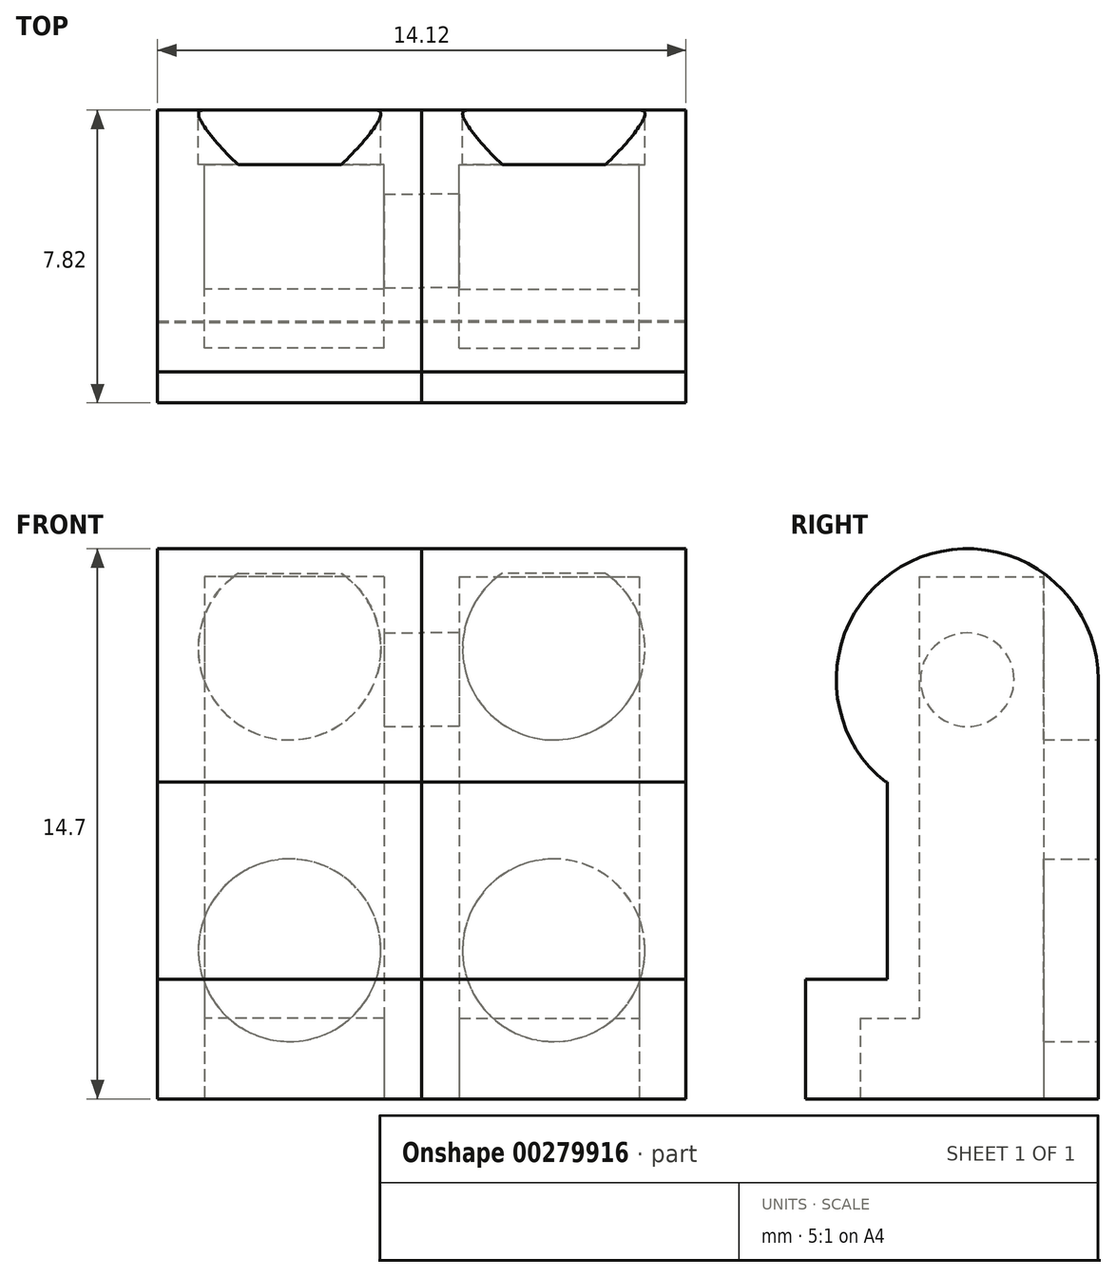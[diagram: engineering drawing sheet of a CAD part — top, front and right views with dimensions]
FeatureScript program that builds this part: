
annotation { "Feature Type Name" : "Feature", "Feature Type Description" : "" }
export const myFeature = defineFeature(function(context is Context, id is Id, definition is map)
    precondition{}
    {
        {
            var Q0;
            Q0=qCreatedBy(makeId("Right.planeOp"),FACE);
            var sketch = newSketch(context, id + "F0", { "sketchPlane" : qUnion([Q0])});
            skLineSegment(sketch, "E0.bottom", {"start": v(-3.9, 7.35) * mm, "end": v(3.91, 7.35) * mm});
            skLineSegment(sketch, "E0.top", {"start": v(-3.91, -7.35) * mm, "end": v(3.9, -7.35) * mm});
            skLineSegment(sketch, "E0.left", {"start": v(-3.9, 7.35) * mm, "end": v(-3.91, -7.35) * mm});
            skLineSegment(sketch, "E0.right", {"start": v(3.91, 7.35) * mm, "end": v(3.9, -7.35) * mm});
            skPoint(sketch, "E0.middle", {"position": v(0, 0) * mm});
            skCircle(sketch, "E1", {"center": v(0.41, 3.85) * mm, "radius": 3.5 * mm});
            skLineSegment(sketch, "E2.bottom", {"start": v(-3.91, 1.11) * mm, "end": v(-1.73, 1.11) * mm});
            skLineSegment(sketch, "E2.top", {"start": v(-3.91, -4.16) * mm, "end": v(-1.73, -4.16) * mm});
            skLineSegment(sketch, "E2.left", {"start": v(-3.9, 1.11) * mm, "end": v(-3.9, -4.16) * mm});
            skLineSegment(sketch, "E2.right", {"start": v(-1.73, 1.11) * mm, "end": v(-1.73, -4.16) * mm});
            skSolve(sketch);
        }
        {
            var Q0;
            {var subQ0=sQuery(id+"F0.wireOp",EDGE,"E1");var subQ4=makeQuery(id+"F0.imprint","INTERSECT",VERTEX,{"derivedFrom":[sQuery(id+"F0.wireOp",EDGE,"E0.bottom"),subQ0]});Q0=makeQuery(id+"F0.imprint","IMPRINT",FACE,{"disambiguationData":[TD([[makeQuery(id+"F0.imprint","IMPRINT",EDGE,{"disambiguationData":[TD([[subQ4,1.0]])],"derivedFrom":subQ0}),1.0]])]});}
            var Q1;
            {var subQ5=sQuery(id+"F0.wireOp",EDGE,"E0.top");Q1=makeQuery(id+"F0.imprint","IMPRINT",FACE,{"disambiguationData":[TD([[makeQuery(id+"F0.imprint","IMPRINT",EDGE,{"derivedFrom":subQ5}),1.0]])]});}
            extrude(context, id + "F1", {"entities" : qUnion([Q0, Q1]), "depth" : 7.06 * mm});
        }
        {
            var Q0;
            Q0=makeQuery(id+"F1.opExtrude","SWEPT_FACE",FACE,{"disambiguationData":[OSD([sQuery(id+"F0.wireOp",EDGE,"E0.top")])]});
            var sketch = newSketch(context, id + "F2", { "sketchPlane" : qUnion([Q0])});
            skLineSegment(sketch, "E3.bottom", {"start": v(1, 2.45) * mm, "end": v(5.81, 2.45) * mm});
            skLineSegment(sketch, "E3.top", {"start": v(1, -2.45) * mm, "end": v(5.81, -2.45) * mm});
            skLineSegment(sketch, "E3.left", {"start": v(1, 2.45) * mm, "end": v(1, -2.45) * mm});
            skLineSegment(sketch, "E3.right", {"start": v(5.81, 2.45) * mm, "end": v(5.81, -2.45) * mm});
            skPoint(sketch, "E3.middle", {"position": v(3.4, 0) * mm});
            skSolve(sketch);
        }
        {
            var Q0;
            Q0=makeQuery(id+"F2.imprint","IMPRINT",FACE,{"disambiguationData":[TD([[makeQuery(id+"F2.imprint","IMPRINT",EDGE,{"derivedFrom":sQuery(id+"F2.wireOp",EDGE,"E3.bottom")}),-1.0]])]});
            extrude(context, id + "F3", {"entities" : qUnion([Q0]), "operationType" : NewBodyOperationType.REMOVE, "oppositeDirection" : true, "depth" : 2.15 * mm});
        }
        {
            var Q0;
            Q0=makeQuery(id+"F1.opExtrude","SWEPT_FACE",FACE,{"disambiguationData":[OSD([sQuery(id+"F0.wireOp",EDGE,"E0.right")])]});
            var sketch = newSketch(context, id + "F4", { "sketchPlane" : qUnion([Q0])});
            skCircle(sketch, "E4", {"center": v(-3.53, -3.38) * mm, "radius": 2.44 * mm});
            skPoint(sketch, "E4.centerSnap0", {"position": v(-3.53, -7.35) * mm});
            skCircle(sketch, "E5", {"center": v(-3.53, 4.68) * mm, "radius": 2.44 * mm});
            skSolve(sketch);
        }
        {
            var Q0;
            Q0=makeQuery(id+"F4.imprint","IMPRINT",FACE,{"disambiguationData":[TD([[makeQuery(id+"F4.imprint","IMPRINT",EDGE,{"derivedFrom":sQuery(id+"F4.wireOp",EDGE,"E4")}),1.0]])]});
            var Q1;
            {var subQ0=sQuery(id+"F4.wireOp",EDGE,"E5");var subQ1=makeQuery(id+"F1.opExtrude","SWEPT_EDGE",EDGE,{"disambiguationData":[OSD([sQuery(id+"F0.wireOp",EDGE,"E0.right"),sQuery(id+"F0.wireOp",EDGE,"E1")])]});var subQ2=makeQuery(id+"F4.imprint","INTERSECT",VERTEX,{"disambiguationData":[OD(0.0)],"derivedFrom":[subQ1,subQ0]});Q1=makeQuery(id+"F4.imprint","IMPRINT",FACE,{"disambiguationData":[TD([[makeQuery(id+"F4.imprint","IMPRINT",EDGE,{"disambiguationData":[TD([[subQ2,-1.0]])],"derivedFrom":subQ0}),1.0]])]});}
            var Q2;
            {var subQ0=sQuery(id+"F4.wireOp",EDGE,"E5");var subQ1=makeQuery(id+"F1.opExtrude","SWEPT_EDGE",EDGE,{"disambiguationData":[OSD([sQuery(id+"F0.wireOp",EDGE,"E0.right"),sQuery(id+"F0.wireOp",EDGE,"E1")])]});var subQ2=makeQuery(id+"F4.imprint","INTERSECT",VERTEX,{"disambiguationData":[OD(0.0)],"derivedFrom":[subQ1,subQ0]});Q2=makeQuery(id+"F4.imprint","IMPRINT",FACE,{"disambiguationData":[TD([[makeQuery(id+"F4.imprint","IMPRINT",EDGE,{"disambiguationData":[TD([[subQ2,1.0]])],"derivedFrom":subQ0}),1.0]])]});}
            extrude(context, id + "F5", {"entities" : qUnion([Q0, Q1, Q2]), "operationType" : NewBodyOperationType.REMOVE, "oppositeDirection" : true, "depth" : 1.46 * mm});
        }
        {
            var Q0;
            Q0=makeQuery(id+"F3.boolean.opBoolean","COPY",FACE,{"derivedFrom":makeQuery(id+"F3.opExtrude","CAP_FACE",FACE,{"disambiguationData":[OSD([sQuery(id+"F2.wireOp",EDGE,"E3.bottom"),sQuery(id+"F2.wireOp",EDGE,"E3.top"),sQuery(id+"F2.wireOp",EDGE,"E3.left"),sQuery(id+"F2.wireOp",EDGE,"E3.right")])],"isStart":false})});
            var sketch = newSketch(context, id + "F6", { "sketchPlane" : qUnion([Q0])});
            skLineSegment(sketch, "E6.bottom", {"start": v(1, -2.45) * mm, "end": v(5.81, -2.45) * mm});
            skLineSegment(sketch, "E6.top", {"start": v(1, 0.88) * mm, "end": v(5.81, 0.88) * mm});
            skLineSegment(sketch, "E6.left", {"start": v(1, -2.45) * mm, "end": v(1, 0.88) * mm});
            skLineSegment(sketch, "E6.right", {"start": v(5.81, -2.45) * mm, "end": v(5.81, 0.88) * mm});
            skSolve(sketch);
        }
        {
            var Q0;
            Q0=makeQuery(id+"F6.imprint","IMPRINT",FACE,{"disambiguationData":[TD([[makeQuery(id+"F6.imprint","IMPRINT",EDGE,{"derivedFrom":sQuery(id+"F6.wireOp",EDGE,"E6.top")}),-1.0]])]});
            extrude(context, id + "F7", {"entities" : qUnion([Q0]), "operationType" : NewBodyOperationType.REMOVE, "oppositeDirection" : true, "depth" : 11.8 * mm});
        }
        {
            var Q0;
            Q0=makeQuery(id+"F1.opExtrude","CAP_FACE",FACE,{"disambiguationData":[OSD([sQuery(id+"F0.wireOp",EDGE,"E0.top"),sQuery(id+"F0.wireOp",EDGE,"E0.left"),sQuery(id+"F0.wireOp",EDGE,"E0.right"),sQuery(id+"F0.wireOp",EDGE,"E1"),sQuery(id+"F0.wireOp",EDGE,"E2.bottom"),sQuery(id+"F0.wireOp",EDGE,"E2.top"),sQuery(id+"F0.wireOp",EDGE,"E2.right")])],"isStart":true});
            var sketch = newSketch(context, id + "F8", { "sketchPlane" : qUnion([Q0])});
            skCircle(sketch, "E7", {"center": v(-0.41, 3.85) * mm, "radius": 1.25 * mm});
            skSolve(sketch);
        }
        {
            var Q0;
            Q0=makeQuery(id+"F8.imprint","IMPRINT",FACE,{"disambiguationData":[TD([[makeQuery(id+"F8.imprint","IMPRINT",EDGE,{"derivedFrom":sQuery(id+"F8.wireOp",EDGE,"E7")}),1.0]])]});
            extrude(context, id + "F9", {"entities" : qUnion([Q0]), "operationType" : NewBodyOperationType.REMOVE, "oppositeDirection" : true, "depth" : 1.25 * mm});
        }
        {
            var Q0;
            Q0=makeQuery(id+"F1.opExtrude","SWEPT_BODY",BODY,{"disambiguationData":[OSD([sQuery(id+"F0.wireOp",EDGE,"E0.top"),sQuery(id+"F0.wireOp",EDGE,"E0.left"),sQuery(id+"F0.wireOp",EDGE,"E0.right"),sQuery(id+"F0.wireOp",EDGE,"E1"),sQuery(id+"F0.wireOp",EDGE,"E2.bottom"),sQuery(id+"F0.wireOp",EDGE,"E2.top"),sQuery(id+"F0.wireOp",EDGE,"E2.right")])]});
            var Q1;
            Q1=qCreatedBy(makeId("Right.planeOp"),FACE);
            mirror(context, id + "F10", {"entities" : qUnion([Q0]), "mirrorPlane" : qUnion([Q1])});
        }
    });
